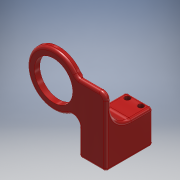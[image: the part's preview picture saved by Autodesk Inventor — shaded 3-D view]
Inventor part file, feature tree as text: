
AUTODESK INVENTOR PART (.ipt)
format: ipt  version: 2018.3 (Build 223284000, 284)  size: 283,136 bytes
history: native  units: mm
features: extrude x6, fillet x6, sketch x6, plane x1
ambient origin geometry x8: Origin, YZ Plane, XZ Plane, XY Plane, X Axis, Y Axis, Z Axis, Center Point
bodies: Solid1 (feature_tree)
feature tree (19):
  extrude  "Extrusion1"  Depth=5.5mm
  plane  "Work Plane1"
  extrude  "Extrusion2"  Depth=4.0mm
  extrude  "Extrusion3"  Depth=19.0mm TaperAngle=0.0deg
  extrude  "Extrusion4"  Depth=5.0mm
  fillet  "Fillet3"  Radius=31.0mm
  fillet  "Fillet4"  Radius=5.0mm
  extrude  "Extrusion5"  Depth=5.0mm
  fillet  "Fillet6"  Radius=4.0mm
  fillet  "Fillet7"  Radius=4.0mm
  fillet  "Fillet8"  Radius=10.0mm
  fillet  "Fillet9"  Radius=10.0mm
  extrude  "Extrusion6"  Depth=5.0mm
  sketch  "Sketch1"  dims[d0=28.5mm d1=5.5mm]
  sketch  "Sketch2"  dims[d2=4.0mm d3=0.0mm d4=50.0mm]
  sketch  "Sketch3"  dims[d5=1.0mm d6=0.0mm d8=19.0mm d9=0.0mm]
  sketch  "Sketch4"  dims[d10=40.0mm d11=15.0mm d12=31.0mm d13=0.0mm d15=5.0mm]
  sketch  "Sketch5"  dims[d16=2.0mm d18=5.0mm d19=4.0mm d20=4.0mm d21=10.0mm d22=10.0mm d23=0.0mm]
  sketch  "Sketch6"  dims[d25=15.0mm d26=5.0mm d27=2.0mm d28=2.0mm d29=4.0mm d30=7.5mm d31=90.0deg d32=4.0mm d33=0.0mm]
